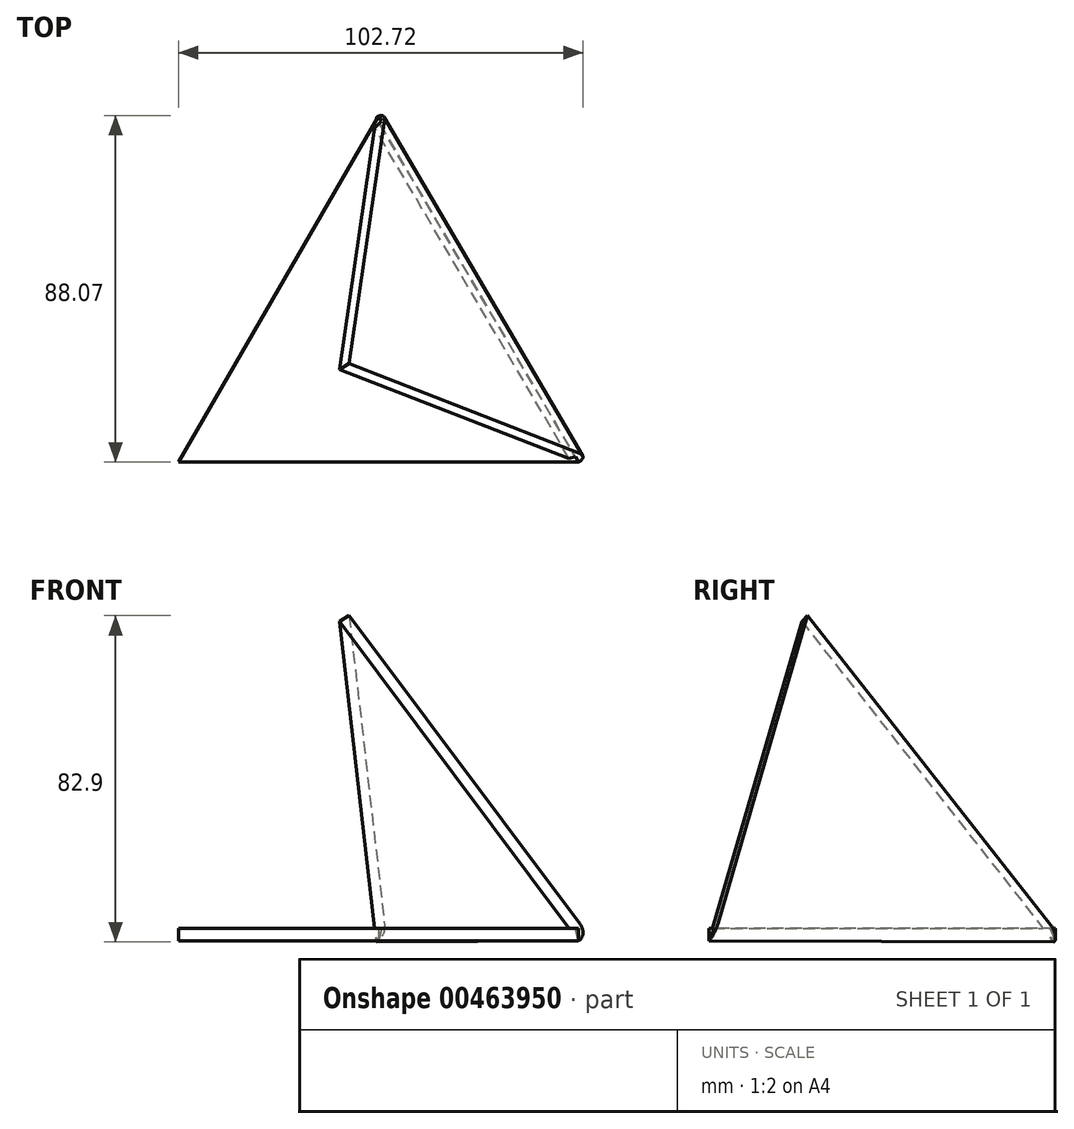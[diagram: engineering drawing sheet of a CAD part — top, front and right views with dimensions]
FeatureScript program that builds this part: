
annotation { "Feature Type Name" : "Feature", "Feature Type Description" : "" }
export const myFeature = defineFeature(function(context is Context, id is Id, definition is map)
    precondition{}
    {
        {
            var Q0;
            Q0=qCreatedBy(makeId("Top.planeOp"),FACE);
            var sketch = newSketch(context, id + "F0", { "sketchPlane" : qUnion([Q0])});
            skLineSegment(sketch, "E0", {"start": v(0, 87.99) * mm, "end": v(-50.8, 0) * mm});
            skLineSegment(sketch, "E1", {"start": v(-50.8, 0) * mm, "end": v(50.8, 0) * mm});
            skLineSegment(sketch, "E2", {"start": v(50.8, 0) * mm, "end": v(0, 87.99) * mm});
            skSolve(sketch);
        }
        {
            var Q0;
            Q0=makeQuery(id+"F0.imprint","IMPRINT",FACE,{"disambiguationData":[TD([[makeQuery(id+"F0.imprint","IMPRINT",EDGE,{"derivedFrom":sQuery(id+"F0.wireOp",EDGE,"E0")}),1.0]])]});
            extrude(context, id + "F1", {"entities" : qUnion([Q0]), "depth" : 3.17 * mm});
        }
        {
            var Q0;
            Q0=qCreatedBy(makeId("Front.planeOp"),FACE);
            var sketch = newSketch(context, id + "F2", { "sketchPlane" : qUnion([Q0])});
            skLineSegment(sketch, "E3", {"start": v(-50.8, 0) * mm, "end": v(0, 87.99) * mm});
            skLineSegment(sketch, "E4", {"start": v(0, 87.99) * mm, "end": v(50.8, 0) * mm});
            skLineSegment(sketch, "E5", {"start": v(-50.8, 0) * mm, "end": v(50.8, 0) * mm});
            skSolve(sketch);
        }
        {
            var Q0;
            Q0=qCreatedBy(makeId("Front.planeOp"),FACE);
            var Q1;
            Q1=sQuery(id+"F2.wireOp",EDGE,"E4");
            cPlane(context, id + "F3", {"entities" : qUnion([Q0, Q1]), "cplaneType" : CPlaneType.LINE_ANGLE, "offset" : 25.4 * mm, "angle" : 63 * degree, "width" : 152.4 * mm, "height" : 152.4 * mm});
        }
        {
            var Q0;
            Q0=qCreatedBy(id+"F3.planeOp",FACE);
            var sketch = newSketch(context, id + "F4", { "sketchPlane" : qUnion([Q0])});
            skLineSegment(sketch, "E6", {"start": v(-19.98, -25.4) * mm, "end": v(6.5, 75.25) * mm});
            skLineSegment(sketch, "E7", {"start": v(6.5, 75.25) * mm, "end": v(78.4, 0) * mm});
            skLineSegment(sketch, "E8", {"start": v(-19.98, -25.4) * mm, "end": v(78.4, 0) * mm});
            skSolve(sketch);
        }
        {
            var Q0;
            Q0 = qSketchRegion(id + "F4", true);
            extrude(context, id + "F5", {"entities" : qUnion([Q0]), "operationType" : NewBodyOperationType.ADD, "depth" : 3.17 * mm});
        }
        {
            var Q0;
            Q0=makeQuery(id+"F5.opExtrude","CAP_EDGE",EDGE,{"disambiguationData":[OSD([sQuery(id+"F4.wireOp",EDGE,"E8")])],"isStart":false});
            fillet(context, id + "F6", {"entities" : qUnion([Q0]), "radius" : 3.17 * mm, "tangentPropagation" : true, "allowEdgeOverflow" : false});
        }
    });
